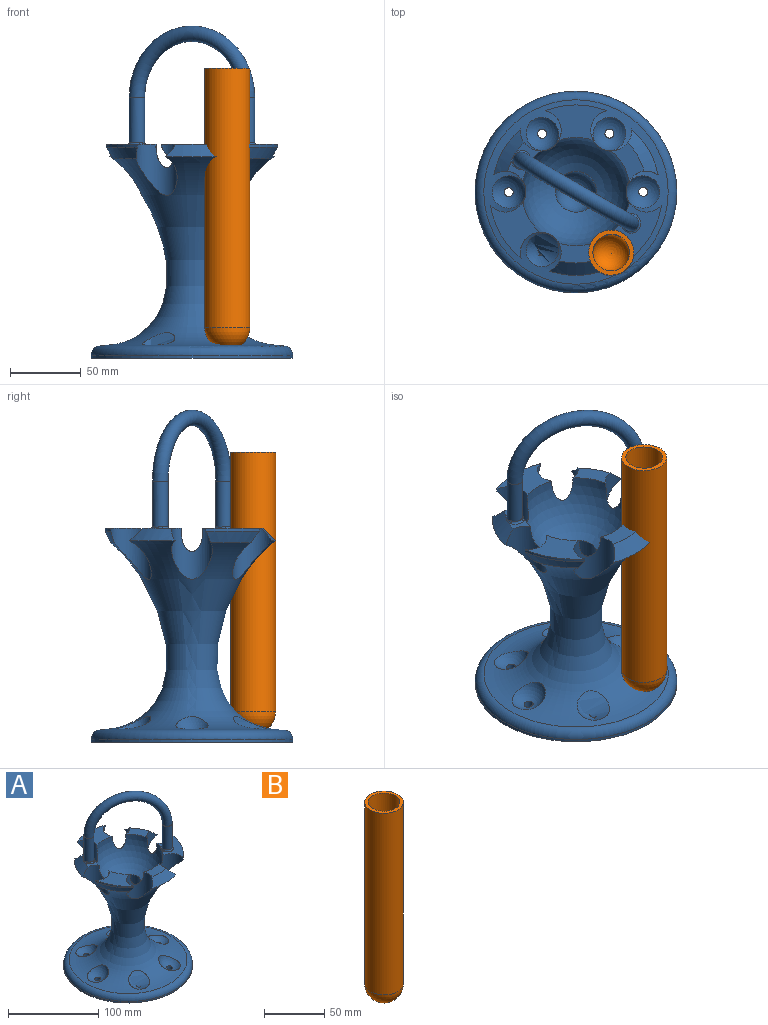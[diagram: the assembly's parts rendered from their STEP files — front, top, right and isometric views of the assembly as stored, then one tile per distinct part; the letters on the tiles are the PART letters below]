
ASSEMBLY  parts=2 mates=1
PART A: 151 faces, bbox 416x416x500.9 mm
  f0: cylinder r=60mm len=16.7mm, axis (0,0,1), area 3.3mm2, adj f4,f104,f121,f147
  f1: cylinder r=60mm len=9.82mm, axis (0,0,1), area 2mm2, adj f17,f116,f119,f137
  f2: plane 11.17x9.29mm, normal (0,0,-1), area 86.1mm2, adj f5,f26,f94,f133
  f3: plane 10.51x8.33mm, normal (0,0,-1), area 36.5mm2, adj f7,f29,f100,f149
  f4: plane 21.17x16.7mm, normal (0,0,-1), area 210.2mm2, adj f0,f8,f104,f147
  f5: sphere r=40mm, area 1214.2mm2, adj f2,f13,f94,f112,f133,f138
  f6: sphere r=40mm, area 1988.1mm2, adj f14,f15,f17,f86,f103,f106,f107,f116
  f7: sphere r=40mm, area 1996.7mm2, adj f3,f12,f16,f93,f96,f97,f100,f128
  f8: sphere r=40mm, area 1214.2mm2, adj f4,f99,f104,f111,f147,f150
  f9: revolved ~135.8x90.85mm, area 7857.1mm2, adj f18,f29,f97,f98,f100,f101,f117,f118
  f10: revolved ~135.8x59.32mm, area 4801mm2, adj f18,f26,f27,f92,f94,f133,f138
  f11: revolved ~135.8x130.56mm, area 42790.2mm2, adj f18,f28,f107,f108,f115,f116,f119,f120
  f12: cylinder r=16mm len=93.34mm, axis (0,0,1), area 1299.2mm2, adj f7,f21,f134,f136
  f13: cylinder r=16mm len=93.34mm, axis (0,0,1), area 1588.5mm2, adj f5,f22,f133,f138
  f14: cylinder r=16mm len=93.34mm, axis (0,0,1), area 1383.8mm2, adj f6,f23,f137,f141
  f15: cylinder r=16mm len=93.34mm, axis (0,0,1), area 1299.2mm2, adj f6,f24,f140,f148
  f16: cylinder r=16mm len=93.34mm, axis (0,0,1), area 1383.8mm2, adj f7,f25,f142,f149
  f17: plane 21.51x12.35mm, normal (0,0,-1), area 99.9mm2, adj f1,f6,f116,f137
  f18: torus R=65mm, axis (0,0,1), area 2610.4mm2, adj f9,f10,f11,f20,f133,f134,f135,f137
  f19: cylinder r=70mm len=63.05mm, axis (0,0,1), area 159mm2, adj f66,f113,f147,f150
  f20: cylinder r=70mm len=140mm, axis (0,0,1), area 714.6mm2, adj f18,f66,f148,f149
  f21: sphere r=16mm, area 136.2mm2, adj f12,f134,f136
  f22: sphere r=16mm, area 167.7mm2, adj f13,f133,f138
  f23: sphere r=16mm, area 186.8mm2, adj f14,f137,f141
  f24: sphere r=16mm, area 136.2mm2, adj f15,f140,f148
  f25: sphere r=16mm, area 145.4mm2, adj f16,f142,f149
  f26: cone r=50mm half-angle=45deg, axis (0,0,-1), area 117.8mm2, adj f2,f10,f94,f133
  f27: cone r=60mm half-angle=25deg, axis (0,0,1), area 181.1mm2, adj f10,f94,f109,f138
  f28: cone r=60mm half-angle=25deg, axis (0,0,1), area 126.9mm2, adj f11,f102,f107,f148
  f29: cone r=50mm half-angle=45deg, axis (0,0,-1), area 57.5mm2, adj f3,f9,f100,f149
  f30: plane 9.4x9.4mm, normal (0,0,-1), area 37.2mm2, adj f37,f87
  f31: plane 9.4x9.4mm, normal (0,0,-1), area 37.2mm2, adj f38,f88
  f32: plane 9.4x9.4mm, normal (0,0,-1), area 37.2mm2, adj f39,f89
  f33: plane 9.4x9.4mm, normal (0,0,-1), area 37.2mm2, adj f40,f90
  f34: plane 9.4x9.4mm, normal (0,0,-1), area 37.2mm2, adj f41,f91
  f35: plane 9.4x9.4mm, normal (0,0,-1), area 37.2mm2, adj f76,f123
  f36: plane 15.41x15.19mm, normal (0,0,1), area 61.6mm2, adj f59,f69,f73,f82,f83,f85
  f37: cylinder r=3.2mm len=6.56mm, axis (0,0,-1), area 121.4mm2, adj f30,f48
  f38: cylinder r=3.2mm len=6.56mm, axis (0,0,-1), area 121.4mm2, adj f31,f51
  f39: cylinder r=3.2mm len=6.56mm, axis (0,0,-1), area 121.5mm2, adj f32,f55
  f40: cylinder r=3.2mm len=6.56mm, axis (0,0,-1), area 121.4mm2, adj f33,f58
  f41: cylinder r=3.2mm len=6.56mm, axis (0,0,-1), area 121.4mm2, adj f34,f68
  f42: sphere r=14.5mm, area 563.3mm2, adj f61,f76
  f43: plane 24.41x14.14mm, normal (0,0,1), area 269.6mm2, adj f44,f47,f59,f71
  f44: cylinder r=14.5mm len=36.11mm, axis (0,0,-1), area 1204mm2, adj f43,f59,f60,f61,f63,f71,f72
  f45: cylinder r=61.5mm len=37.94mm, axis (0,0,1), area 90.9mm2, adj f46,f47,f50,f70
  f46: plane 41.97x37.16mm, normal (0,0,1), area 461.8mm2, adj f45,f47,f50,f59,f80,f81
  f47: cylinder r=14.5mm len=36.11mm, axis (0,0,-1), area 1203.9mm2, adj f43,f45,f46,f59,f61,f70,f71
  f48: sphere r=14.5mm, area 562.3mm2, adj f37,f61
  f49: plane 27.14x23.03mm, normal (0,0,1), area 269.6mm2, adj f50,f54,f59,f75
  f50: cylinder r=14.5mm len=36.11mm, axis (0,0,-1), area 1203.8mm2, adj f45,f46,f49,f59,f61,f70,f75
  f51: sphere r=14.5mm, area 562.3mm2, adj f38,f61
  f52: cylinder r=61.5mm len=43.81mm, axis (0,0,1), area 90.9mm2, adj f53,f54,f57,f74
  f53: plane 43.81x25.02mm, normal (0,0,1), area 616.2mm2, adj f52,f54,f57,f59
  f54: cylinder r=14.5mm len=36.11mm, axis (0,0,-1), area 1203.9mm2, adj f49,f52,f53,f59,f61,f74,f75
  f55: sphere r=14.5mm, area 562.3mm2, adj f39,f61
  f56: plane 17.61x14.33mm, normal (0,0,1), area 61.6mm2, adj f57,f59,f73,f82,f84,f85
  f57: cylinder r=14.5mm len=36.11mm, axis (0,0,-1), area 1204mm2, adj f52,f53,f56,f59,f61,f73,f74
  f58: sphere r=14.5mm, area 562.3mm2, adj f40,f61
  f59: sphere r=38.5mm, area 7731.3mm2, adj f36,f43,f44,f46,f47,f49,f50,f53
  f60: cylinder r=61.5mm len=37.94mm, axis (0,0,1), area 90.9mm2, adj f44,f63,f69,f72
  f61: revolved ~134.19x130.57mm, area -43002.6mm2, adj f42,f44,f47,f48,f50,f51,f54,f55
  f62: cylinder r=14.5mm len=94.34mm, axis (0,0,1), area 8594.5mm2, adj f59,f67
  f63: plane 40.03x35.23mm, normal (0,0,1), area 616.2mm2, adj f44,f59,f60,f69
  f64: torus R=65mm, axis (0,0,1), area 4271.5mm2, adj f61,f65
  f65: cylinder r=71.5mm len=143mm, axis (0,0,1), area 898.5mm2, adj f64,f66
  f66: plane 143x143mm, normal (0,0,-1), area 1183mm2, adj f19,f20,f65,f133,f134,f135,f136,f137
  f67: sphere r=14.5mm, area 1321mm2, adj f62
  f68: sphere r=14.5mm, area 562.3mm2, adj f41,f61
  f69: cylinder r=14.5mm len=36.11mm, axis (0,0,-1), area 1204.1mm2, adj f36,f59,f60,f61,f63,f72,f73
  f70: cone r=61.36mm half-angle=25deg, axis (0,0,1), area 357.3mm2, adj f45,f47,f50,f61
  f71: cone r=51.06mm half-angle=45deg, axis (0,0,-1), area 383.6mm2, adj f43,f44,f47,f61
  f72: cone r=61.36mm half-angle=25deg, axis (0,0,1), area 357.3mm2, adj f44,f60,f61,f69
  f73: cone r=51.06mm half-angle=45deg, axis (0,0,-1), area 383.6mm2, adj f36,f56,f57,f61,f69,f82
  f74: cone r=61.36mm half-angle=25deg, axis (0,0,1), area 357.3mm2, adj f52,f54,f57,f61
  f75: cone r=51.06mm half-angle=45deg, axis (0,0,-1), area 383.6mm2, adj f49,f50,f54,f61
  f76: cylinder r=3.2mm len=6.56mm, axis (0,0,-1), area 121.5mm2, adj f35,f42
  f77: cylinder r=5.5mm len=32mm, axis (0,0,1), area 1105.8mm2, adj f78,f82,f83,f84,f85
  f78: torus R=45mm, axis (0.5,0.87,0), area 4885.5mm2, adj f77,f79
  f79: cylinder r=5.5mm len=32.76mm, axis (0,0,-1), area 1108.9mm2, adj f78,f80,f81
  f80: torus R=7mm, axis (0,0,-1), area 69mm2, adj f46,f79,f81
  f81: bspline ~8.69x5.59mm, area 15.4mm2, adj f46,f59,f79,f80
  f82: bspline ~9.4x5.76mm, area 16.4mm2, adj f36,f56,f73,f77,f83,f84
  f83: torus R=7mm, axis (0,0,-1), area 22.7mm2, adj f36,f77,f82,f85
  f84: torus R=7mm, axis (0,0,-1), area 22.7mm2, adj f56,f77,f82,f85
  f85: bspline ~9.09x6.13mm, area 14.7mm2, adj f36,f56,f59,f77,f83,f84
  f86: plane 10.72x9.34mm, normal (0,0,-1), area 30.1mm2, adj f6,f116,f120,f130
  f87: cylinder r=4.7mm len=9.4mm, axis (0,0,-1), area 164.8mm2, adj f30,f98
  f88: cylinder r=4.7mm len=9.4mm, axis (0,0,-1), area 164.8mm2, adj f31,f101
  f89: cylinder r=4.7mm len=9.4mm, axis (0,0,-1), area 164.8mm2, adj f32,f105
  f90: cylinder r=4.7mm len=9.4mm, axis (0,0,-1), area 164.8mm2, adj f33,f108
  f91: cylinder r=4.7mm len=9.4mm, axis (0,0,-1), area 164.8mm2, adj f34,f115
  f92: sphere r=16mm, area 636.9mm2, adj f10,f123
  f93: plane 11.17x9.29mm, normal (0,0,-1), area 86.1mm2, adj f7,f97,f118,f134
  f94: cylinder r=16mm len=34.18mm, axis (0,0,-1), area 901.5mm2, adj f2,f5,f10,f26,f27,f109,f112
  f95: cylinder r=60mm len=30.22mm, axis (0,0,1), area 7mm2, adj f96,f97,f100,f117
  f96: plane 32.75x29.64mm, normal (0,0,-1), area 309.1mm2, adj f7,f95,f97,f100,f127
  f97: cylinder r=16mm len=34.18mm, axis (0,0,-1), area 900.9mm2, adj f7,f9,f93,f95,f96,f117,f118
  f98: sphere r=16mm, area 590.4mm2, adj f9,f87
  f99: plane 16.68x16.44mm, normal (0,0,-1), area 135.7mm2, adj f8,f104,f122,f150
  f100: cylinder r=16mm len=34.18mm, axis (0,0,-1), area 901.5mm2, adj f3,f7,f9,f29,f95,f96,f117
  f101: sphere r=16mm, area 590.4mm2, adj f9,f88
  f102: cylinder r=60mm len=16.7mm, axis (0,0,1), area 3.3mm2, adj f28,f103,f107,f148
  f103: plane 21.17x16.7mm, normal (0,0,-1), area 210.2mm2, adj f6,f102,f107,f148
  f104: cylinder r=16mm len=34.18mm, axis (0,0,-1), area 900.9mm2, adj f0,f4,f8,f99,f110,f121,f122
  f105: sphere r=16mm, area 590.4mm2, adj f89,f110
  f106: plane 11.69x9.33mm, normal (0,0,-1), area 30.1mm2, adj f6,f107,f120,f131
  f107: cylinder r=16mm len=34.18mm, axis (0,0,-1), area 901.5mm2, adj f6,f11,f28,f102,f103,f106,f120
  f108: sphere r=16mm, area 590.4mm2, adj f11,f90
  f109: cylinder r=60mm len=19.03mm, axis (0,0,1), area 4.6mm2, adj f27,f94,f112,f138
  f110: revolved ~135.8x59.32mm, area 4807.5mm2, adj f104,f105,f113,f121,f122,f147,f150
  f111: cylinder r=16mm len=93.34mm, axis (0,0,1), area 1588.5mm2, adj f8,f114,f147,f150
  f112: plane 27.06x25.84mm, normal (0,0,-1), area 320.5mm2, adj f5,f94,f109,f138
  f113: torus R=65mm, axis (0,0,1), area 585.2mm2, adj f19,f110,f147,f150
  f114: sphere r=16mm, area 167.7mm2, adj f111,f147,f150
  f115: sphere r=16mm, area 590.4mm2, adj f11,f91
  f116: cylinder r=16mm len=34.18mm, axis (0,0,-1), area 900.9mm2, adj f1,f6,f11,f17,f86,f119,f120
  f117: cone r=60mm half-angle=25deg, axis (0,0,1), area 266.6mm2, adj f9,f95,f97,f100
  f118: cone r=50mm half-angle=45deg, axis (0,0,-1), area 117.8mm2, adj f9,f93,f97,f134
  f119: cone r=60mm half-angle=25deg, axis (0,0,1), area 72.8mm2, adj f1,f11,f116,f137
  f120: cone r=50mm half-angle=45deg, axis (0,0,-1), area 250.9mm2, adj f11,f86,f106,f107,f116,f129
  f121: cone r=60mm half-angle=25deg, axis (0,0,1), area 126.9mm2, adj f0,f104,f110,f147
  f122: cone r=50mm half-angle=45deg, axis (0,0,-1), area 178mm2, adj f99,f104,f110,f150
  f123: cylinder r=4.7mm len=9.4mm, axis (0,0,-1), area 124mm2, adj f35,f92
  f124: cylinder r=4mm len=32.76mm, axis (0,0,1), area 809.1mm2, adj f125,f129,f130,f131,f132
  f125: torus R=45mm, axis (0.5,0.87,0), area 3553.1mm2, adj f124,f126
  f126: cylinder r=4mm len=32mm, axis (0,0,-1), area 804.2mm2, adj f125,f127,f128
  f127: torus R=7mm, axis (0,0,-1), area 116.2mm2, adj f96,f126,f128
  f128: bspline ~7.99x5.58mm, area 21.6mm2, adj f7,f126,f127
  f129: bspline ~9.42x6.13mm, area 25mm2, adj f120,f124,f130,f131
  f130: torus R=7mm, axis (0,0,-1), area 38.2mm2, adj f86,f124,f129,f132
  f131: torus R=7mm, axis (0,0,-1), area 38.2mm2, adj f106,f124,f129,f132
  f132: bspline ~7.99x5.58mm, area 21.6mm2, adj f6,f124,f130,f131
  f133: plane 155.89x74.72mm, normal (-1,0,0), area 1757mm2, adj f2,f5,f10,f13,f18,f22,f26,f66
  f134: plane 154.8x73.34mm, normal (1,0,0), area 1755.8mm2, adj f7,f9,f12,f18,f21,f66,f93,f118
  f135: plane 2.47x1.5mm, normal (0,-1,0), area 3.7mm2, adj f18,f66,f133,f134
  f136: plane 132.21x30.73mm, normal (-0.57,-0.82,0), area 1035.6mm2, adj f7,f9,f12,f21,f66,f134,f143,f144
  f137: plane 411.23x323.96mm, normal (-0.4,0.92,0), area 1790.3mm2, adj f1,f6,f11,f14,f17,f18,f23,f66
  f138: plane 155.89x68.79mm, normal (0.4,-0.92,0), area 1791.1mm2, adj f5,f10,f13,f18,f22,f27,f66,f109
  f139: plane 3.3x1.41mm, normal (-0.92,-0.4,0), area 4.9mm2, adj f18,f66,f137,f138
  f140: plane 135.88x32.56mm, normal (0.57,0.82,0), area 1103.5mm2, adj f6,f11,f15,f24,f66,f145,f146,f148
  f141: plane 136.2x32.96mm, normal (-0.57,-0.82,0), area 1103.9mm2, adj f6,f11,f14,f23,f66,f137,f145,f146
  f142: plane 132.53x31.13mm, normal (0.57,0.82,0), area 1036mm2, adj f7,f9,f16,f25,f66,f143,f144,f149
  f143: plane 18.23x1.25mm, normal (0.82,-0.57,0), area 27.3mm2, adj f9,f66,f136,f142
  f144: plane 13.25x1.27mm, normal (0.82,-0.57,0), area 19.8mm2, adj f7,f9,f136,f142
  f145: plane 13.35x1.27mm, normal (-0.82,0.57,0), area 19.9mm2, adj f6,f11,f140,f141
  f146: plane 16.53x1.25mm, normal (-0.82,0.57,0), area 24.8mm2, adj f11,f66,f140,f141
  f147: plane 155.89x74.74mm, normal (1,0,0), area 1792.2mm2, adj f0,f4,f8,f19,f66,f110,f111,f113
  f148: plane 375.76x294.32mm, normal (-1,0,0), area 1791mm2, adj f6,f11,f15,f18,f20,f24,f28,f66
  f149: plane 155.12x67.99mm, normal (0.4,-0.92,0), area 1756.2mm2, adj f3,f7,f9,f16,f18,f20,f25,f29
  f150: plane 155.89x68.94mm, normal (-0.4,0.92,0), area 1757mm2, adj f8,f19,f66,f99,f110,f111,f113,f114
PART B: 5 faces, bbox 32x32x200 mm
  f0: cylinder r=16mm len=184mm, axis (0,0,1), area 18497.7mm2, adj f1,f2
  f1: sphere r=16mm, area 1608.5mm2, adj f0
  f2: plane 32x32mm, normal (0,0,1), area 273.3mm2, adj f0,f3
  f3: cylinder r=13mm len=184mm, axis (0,0,1), area 15029.4mm2, adj f2,f4
  f4: sphere r=13mm, area 1061.9mm2, adj f3
PLACE A at identity fixed
PLACE B rot(axis=(0,0,-1),18deg) t=(72.56,-58.72,1.5)mm
MATE cylindrical B.f0 <-> A.f47  axis (0,0,1) through (25,-43.3,113.5)mm
